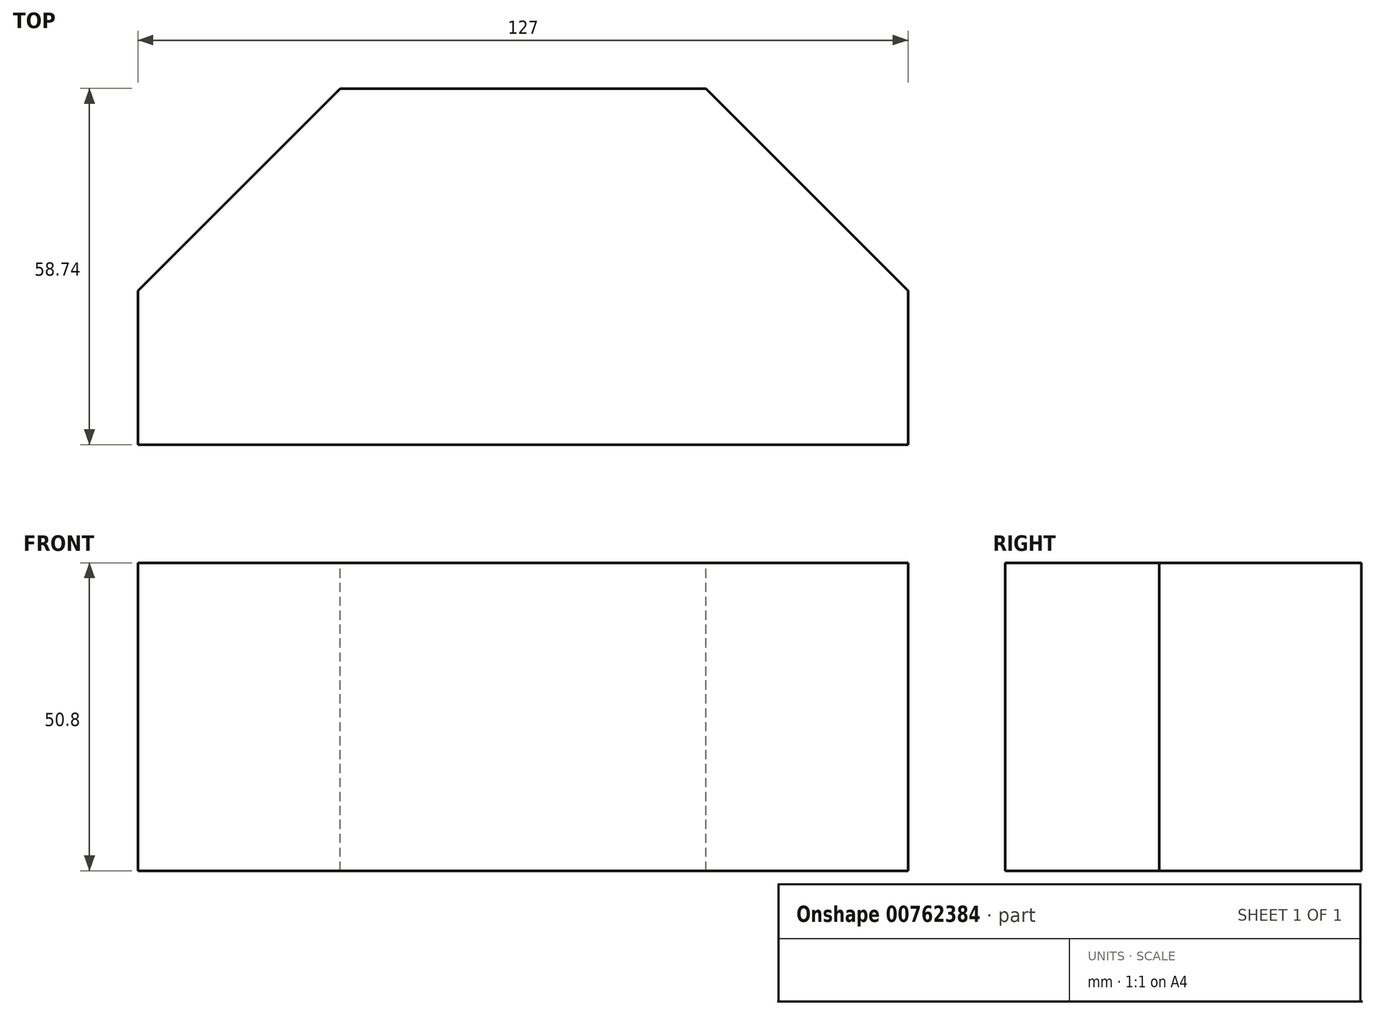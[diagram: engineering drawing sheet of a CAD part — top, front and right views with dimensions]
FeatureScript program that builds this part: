
annotation { "Feature Type Name" : "Feature", "Feature Type Description" : "" }
export const myFeature = defineFeature(function(context is Context, id is Id, definition is map)
    precondition{}
    {
        {
            var Q0;
            Q0=qCreatedBy(makeId("Top.planeOp"),FACE);
            var sketch = newSketch(context, id + "F0", { "sketchPlane" : qUnion([Q0])});
            skLineSegment(sketch, "E0", {"start": v(0, 0) * mm, "end": v(-127, 0) * mm});
            skLineSegment(sketch, "E1", {"start": v(-127, 0) * mm, "end": v(-127, 25.4) * mm});
            skLineSegment(sketch, "E2", {"start": v(-127, 25.4) * mm, "end": v(-93.66, 58.74) * mm});
            skLineSegment(sketch, "E3", {"start": v(-93.66, 58.74) * mm, "end": v(-33.34, 58.74) * mm});
            skLineSegment(sketch, "E4", {"start": v(-33.34, 58.74) * mm, "end": v(0, 25.4) * mm});
            skLineSegment(sketch, "E5", {"start": v(0, 25.4) * mm, "end": v(0, 0) * mm});
            skSolve(sketch);
        }
        {
            var Q0;
            Q0=makeQuery(id+"F0.imprint","IMPRINT",FACE,{"disambiguationData":[TD([[makeQuery(id+"F0.imprint","IMPRINT",EDGE,{"derivedFrom":sQuery(id+"F0.wireOp",EDGE,"E0")}),-1.0]])]});
            extrude(context, id + "F1", {"entities" : qUnion([Q0]), "oppositeDirection" : true, "depth" : 50.8 * mm, "offsetDistance" : 25.4 * mm});
        }
    });
